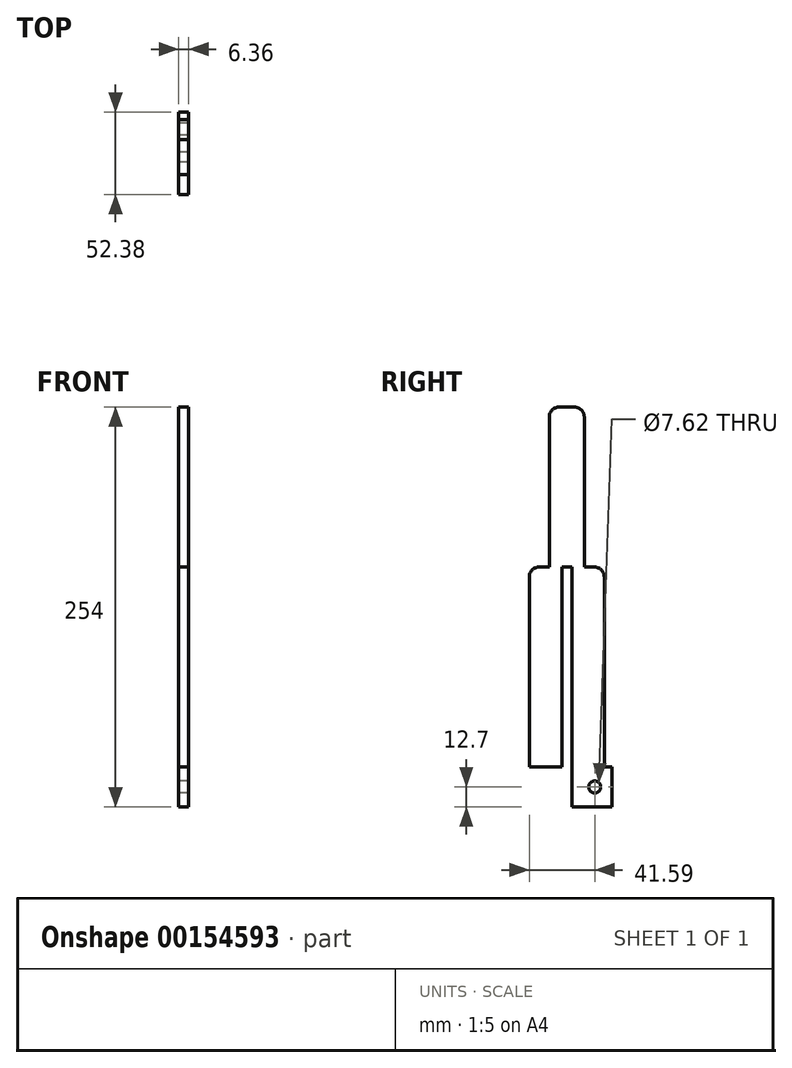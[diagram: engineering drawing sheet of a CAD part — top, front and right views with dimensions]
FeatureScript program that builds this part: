
annotation { "Feature Type Name" : "Feature", "Feature Type Description" : "" }
export const myFeature = defineFeature(function(context is Context, id is Id, definition is map)
    precondition{}
    {
        {
            var Q0;
            Q0=qCreatedBy(makeId("Right.planeOp"),FACE);
            var sketch = newSketch(context, id + "F0", { "sketchPlane" : qUnion([Q0])});
            skLineSegment(sketch, "E0.bottom", {"start": v(23.81, -63.5) * mm, "end": v(3.18, -63.5) * mm});
            skLineSegment(sketch, "E0.top", {"start": v(17.46, 63.5) * mm, "end": v(17.46, 63.5) * mm});
            skLineSegment(sketch, "E0.left", {"start": v(23.81, -63.5) * mm, "end": v(23.81, 57.15) * mm});
            skLineSegment(sketch, "E0.right", {"start": v(-23.81, -63.5) * mm, "end": v(-23.81, 57.15) * mm});
            skPoint(sketch, "E0.middle", {"position": v(0, 0) * mm});
            skLineSegment(sketch, "E1", {"start": v(-11.1, 63.5) * mm, "end": v(-11.1, 158.75) * mm});
            skLineSegment(sketch, "E2", {"start": v(-4.75, 165.1) * mm, "end": v(4.77, 165.1) * mm});
            skLineSegment(sketch, "E3", {"start": v(11.12, 158.75) * mm, "end": v(11.11, 63.5) * mm});
            skLineSegment(sketch, "E4.trimOffspring", {"start": v(-17.45, 63.5) * mm, "end": v(-17.46, 63.5) * mm});
            skPoint(sketch, "E5.start.orphan", {"position": v(0, -63.5) * mm});
            skPoint(sketch, "E6.visualSharp", {"position": v(-11.1, 63.5) * mm});
            skPoint(sketch, "E7.visualSharp", {"position": v(11.11, 63.5) * mm});
            skPoint(sketch, "E8.visualSharp", {"position": v(-23.81, 63.5) * mm});
            skArc(sketch, "E8.filletArc", {"start": v(-17.46, 63.5) * mm, "mid": v(-21.95, 61.64) * mm, "end": v(-23.81, 57.15) * mm});
            skPoint(sketch, "E9.visualSharp", {"position": v(23.81, 63.5) * mm});
            skArc(sketch, "E9.filletArc", {"start": v(23.81, 57.15) * mm, "mid": v(21.95, 61.64) * mm, "end": v(17.46, 63.5) * mm});
            skPoint(sketch, "E10.visualSharp", {"position": v(11.13, 165.1) * mm});
            skArc(sketch, "E10.filletArc", {"start": v(11.12, 158.75) * mm, "mid": v(9.26, 163.24) * mm, "end": v(4.77, 165.1) * mm});
            skPoint(sketch, "E11.visualSharp", {"position": v(-11.1, 165.1) * mm});
            skArc(sketch, "E11.filletArc", {"start": v(-4.75, 165.1) * mm, "mid": v(-9.24, 163.24) * mm, "end": v(-11.1, 158.75) * mm});
            skLineSegment(sketch, "E12", {"start": v(-3.18, -63.5) * mm, "end": v(-3.18, 63.5) * mm});
            skLineSegment(sketch, "E13", {"start": v(-3.18, 63.5) * mm, "end": v(3.17, 63.5) * mm});
            skLineSegment(sketch, "E14", {"start": v(3.17, 63.5) * mm, "end": v(3.17, -63.5) * mm});
            skLineSegment(sketch, "E15.trimOffspring", {"start": v(-3.18, -63.5) * mm, "end": v(-23.81, -63.5) * mm});
            skLineSegment(sketch, "E16.bottom", {"start": v(3.18, -63.5) * mm, "end": v(28.58, -63.5) * mm});
            skLineSegment(sketch, "E16.top", {"start": v(3.18, -88.9) * mm, "end": v(28.58, -88.9) * mm});
            skLineSegment(sketch, "E16.left", {"start": v(3.18, -63.5) * mm, "end": v(3.18, -88.9) * mm});
            skLineSegment(sketch, "E16.right", {"start": v(28.58, -63.5) * mm, "end": v(28.58, -88.9) * mm});
            skCircle(sketch, "E17", {"center": v(17.78, -76.2) * mm, "radius": 3.81 * mm});
            skPoint(sketch, "E17.centerSnap0", {"position": v(28.58, -76.2) * mm});
            skLineSegment(sketch, "E18", {"start": v(-17.45, 63.5) * mm, "end": v(-11.1, 63.5) * mm});
            skLineSegment(sketch, "E19", {"start": v(11.11, 63.5) * mm, "end": v(17.46, 63.5) * mm});
            skSolve(sketch);
        }
        {
            var Q0;
            Q0=qSketchRegion(id+"F0",true);
            extrude(context, id + "F1", {"entities" : qUnion([Q0]), "endBound" : BoundingType.SYMMETRIC, "depth" : 6.35 * mm});
        }
    });
